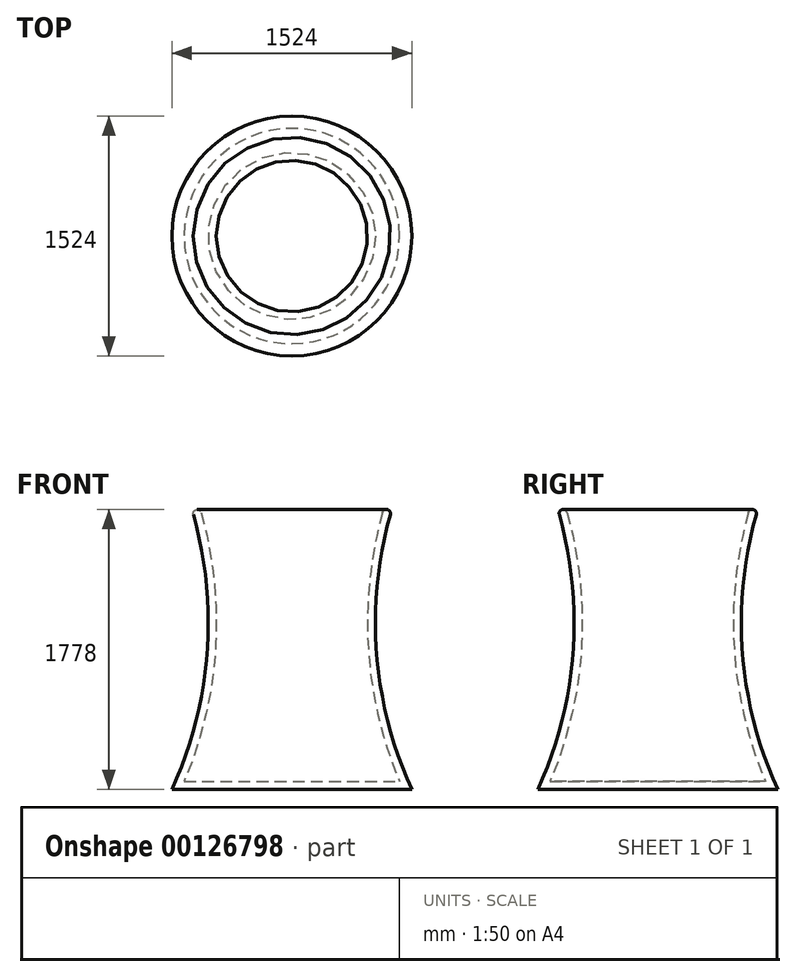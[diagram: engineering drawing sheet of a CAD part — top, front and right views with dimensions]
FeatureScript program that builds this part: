
annotation { "Feature Type Name" : "Feature", "Feature Type Description" : "" }
export const myFeature = defineFeature(function(context is Context, id is Id, definition is map)
    precondition{}
    {
        {
            var Q0;
            Q0=qCreatedBy(makeId("Front.planeOp"),FACE);
            var sketch = newSketch(context, id + "F0", { "sketchPlane" : qUnion([Q0])});
            skLineSegment(sketch, "E0", {"start": v(0, 0) * mm, "end": v(-762, 0) * mm});
            skLineSegment(sketch, "E1", {"start": v(-635, 1778) * mm, "end": v(0, 1778) * mm});
            skLineSegment(sketch, "E2", {"start": v(0, 1778) * mm, "end": v(0, 0) * mm});
            skArc(sketch, "E3", {"start": v(-762, 0) * mm, "mid": v(-537.4, 877.5) * mm, "end": v(-635, 1778) * mm});
            skSolve(sketch);
        }
        {
            var Q0;
            Q0=makeQuery(id+"F0.imprint","IMPRINT",FACE,{"disambiguationData":[TD([[makeQuery(id+"F0.imprint","IMPRINT",EDGE,{"derivedFrom":sQuery(id+"F0.wireOp",EDGE,"E0")}),-1.0]])]});
            var Q1;
            Q1=sQuery(id+"F0.wireOp",EDGE,"E2");
            revolve(context, id + "F1", {"entities" : qUnion([Q0]), "axis" : qUnion([Q1]), "revolveType" : RevolveType.FULL});
        }
        {
            var Q0;
            Q0=makeQuery(id+"F1.opRevolve","SWEPT_FACE",FACE,{"disambiguationData":[OSD([sQuery(id+"F0.wireOp",EDGE,"E1")])]});
            shell(context, id + "F2", {"entities" : qUnion([Q0]), "thickness" : 50.8 * mm});
        }
        {
            var Q0;
            Q0=makeQuery(id+"F2.opShell","OFFSET_EDGE",EDGE,{"disambiguationData":[OSD([sQuery(id+"F0.wireOp",EDGE,"H65kSfoj-Z2HJ-BBUs-Z1aB-DT8R4b92nMfE"),sQuery(id+"F0.wireOp",EDGE,"E1")])]});
            var Q1;
            Q1=makeQuery(id+"F1.opRevolve","SWEPT_EDGE",EDGE,{"disambiguationData":[OSD([sQuery(id+"F0.wireOp",EDGE,"H65kSfoj-Z2HJ-BBUs-Z1aB-DT8R4b92nMfE"),sQuery(id+"F0.wireOp",EDGE,"E1")])]});
            fillet(context, id + "F3", {"entities" : qUnion([Q0, Q1]), "radius" : 25.4 * mm, "tangentPropagation" : true, "allowEdgeOverflow" : false});
        }
    });
